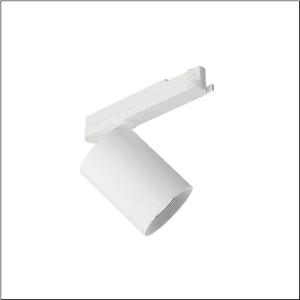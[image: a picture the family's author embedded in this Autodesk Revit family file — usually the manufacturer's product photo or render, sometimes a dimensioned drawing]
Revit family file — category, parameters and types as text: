
# Revit family: spot_11_51sd14mba5a
name_source: partatom
category: Lighting Fixtures
units: mm (PartAtom-declared; Revit-internal decimal feet)

## family parameters
Cut with Voids When Loaded = No
Host = Face
Light Source = No
Part Type = Normal
Room Calculation Point = No
Round Connector Dimension = Use Diameter
Shared = No

## types (1)
- --- (1 x LED, 7210 lm, 50.7 W, 2700K)
    Apparent Load = 51 VA
    CIE Flux Codes = 95 98 100 100 100
    Color Rendering = 90
    Color Temperature = 2700K
    Default Elevation = 1800 mm
    Description = Spot 11, directional spotlight, light control with lens, of PMMA, LED rated luminous flux: 5.550lm, light colour: 927, control gear: ECG Multilumen, with 3-phase adapter, mains connection: 220..240V, AC, 50/60Hz, of aluminium, traffic white (RAL 9016), length: 213mm, diameter: 105mm, protection rating (complete): IP20, insulation class (complete): insulation class I (protective earthing), certification: CE, impact resistance: IK02, permissible ambient temperature for indoor applications: -20..+40°C, packaging unit: 1 piece
    Height = 175 mm
    Lamp = 1 x LED
    Lamp Light Flux = 7210 lm
    Lamp Power = 50.7 W
    Lamp count = 1
    Length = 105 mm
    Luminous efficacy = 142 lm/W
    Manufacturer = Siteco
    ModVariant = No
    Model = 51SD14MBA5A
    Mounting Place = Ceiling
    Mounting Type = Pendant
    Number of Poles = 1
    OnlyDefault = Yes
    Power Factor = 1
    Product Name = Spot 11
    Product group = directional spotlight
    ProductGroupID = 905
    Protection Class = Protection class I
    Protection Degree = IP 20
    RLX_Detail_Level = 1
    RLX_Emergency_Light_Flux = 0 lm
    RLX_Emergency_Type = 0
    RLX_Emergency_Type_DB = No
    RlxData = <blob elided: 17685 chars, md5=ac581140>
    Socket = socket
    Standby Power = 0 W
    System Light Flux = 7210 lm
    System Power = 51 W
    Type Comments = factory setting: luminous flux: 100 % | (ON | ON | ON | ON) | 1050 mA
    Type Image = l_1006697.jpg
    URL = http://relux.com
    VarID = @adj_097671
    Voltage = 0 V
    Weight = 0.00 kg
    Width = 0 mm  [stored 0 ft]

note: [stored X ft] marks values corroborated as IEEE doubles in the binary element streams (Revit-internal decimal feet)

## geometry (parser evidence)
native form markers: Blend x4, Sweep x10
no freeform markers — native parametric forms only
